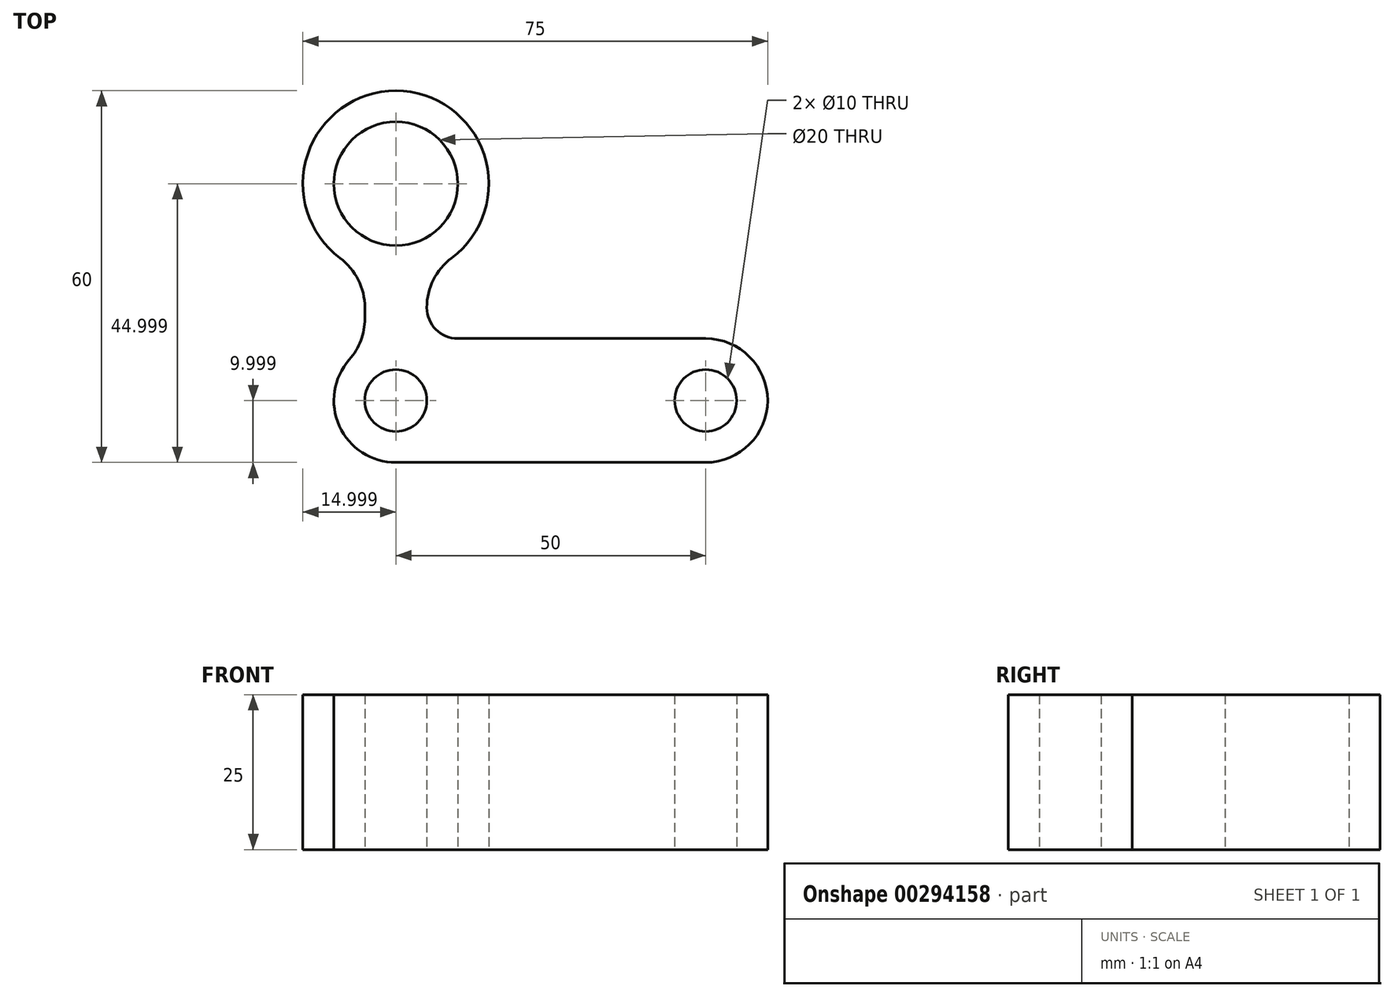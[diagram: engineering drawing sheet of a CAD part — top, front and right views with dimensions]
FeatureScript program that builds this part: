
annotation { "Feature Type Name" : "Feature", "Feature Type Description" : "" }
export const myFeature = defineFeature(function(context is Context, id is Id, definition is map)
    precondition{}
    {
        {
            var Q0;
            Q0=qCreatedBy(makeId("Top.planeOp"),FACE);
            var sketch = newSketch(context, id + "F0", { "sketchPlane" : qUnion([Q0])});
            skLineSegment(sketch, "E0", {"start": v(19.45, -35.12) * mm, "end": v(-30.55, -35.12) * mm});
            skArc(sketch, "E1", {"start": v(19.45, -35.12) * mm, "mid": v(29.45, -25.12) * mm, "end": v(19.45, -15.12) * mm});
            skCircle(sketch, "E2", {"center": v(19.45, -25.12) * mm, "radius": 5 * mm});
            skCircle(sketch, "E3", {"center": v(-30.55, -25.12) * mm, "radius": 5 * mm});
            skCircle(sketch, "E4", {"center": v(-30.55, 9.88) * mm, "radius": 10 * mm});
            skArc(sketch, "E5", {"start": v(-21.55, -2.12) * mm, "mid": v(-30.55, 24.88) * mm, "end": v(-39.55, -2.12) * mm});
            skArc(sketch, "E6", {"start": v(-38.05, -18.5) * mm, "mid": v(-39.67, -29.24) * mm, "end": v(-30.55, -35.12) * mm});
            skLineSegment(sketch, "E7", {"start": v(-35.55, -10.12) * mm, "end": v(-35.55, -11.9) * mm});
            skLineSegment(sketch, "E8", {"start": v(-25.55, -10.12) * mm, "end": v(-25.55, -10.12) * mm});
            skLineSegment(sketch, "E9", {"start": v(-20.55, -15.12) * mm, "end": v(19.45, -15.12) * mm});
            skPoint(sketch, "E10.visualSharp", {"position": v(-35.55, -16.46) * mm});
            skArc(sketch, "E10.filletArc", {"start": v(-38.05, -18.5) * mm, "mid": v(-36.2, -15.43) * mm, "end": v(-35.55, -11.9) * mm});
            skPoint(sketch, "E11.visualSharp", {"position": v(-35.55, -4.26) * mm});
            skArc(sketch, "E11.filletArc", {"start": v(-35.55, -10.12) * mm, "mid": v(-36.6, -5.65) * mm, "end": v(-39.55, -2.12) * mm});
            skPoint(sketch, "E12.visualSharp", {"position": v(-25.55, -4.26) * mm});
            skArc(sketch, "E12.filletArc", {"start": v(-21.55, -2.12) * mm, "mid": v(-24.5, -5.65) * mm, "end": v(-25.55, -10.12) * mm});
            skPoint(sketch, "E13.visualSharp", {"position": v(-25.55, -15.12) * mm});
            skArc(sketch, "E14.filletArc", {"start": v(-25.55, -10.12) * mm, "mid": v(-24.09, -13.66) * mm, "end": v(-20.55, -15.12) * mm});
            skSolve(sketch);
        }
        {
            var Q0;
            Q0=makeQuery(id+"F0.imprint","IMPRINT",FACE,{"disambiguationData":[TD([[makeQuery(id+"F0.imprint","IMPRINT",EDGE,{"derivedFrom":sQuery(id+"F0.wireOp",EDGE,"E0")}),-1.0]])]});
            extrude(context, id + "F1", {"entities" : qUnion([Q0]), "depth" : 25 * mm});
        }
    });
